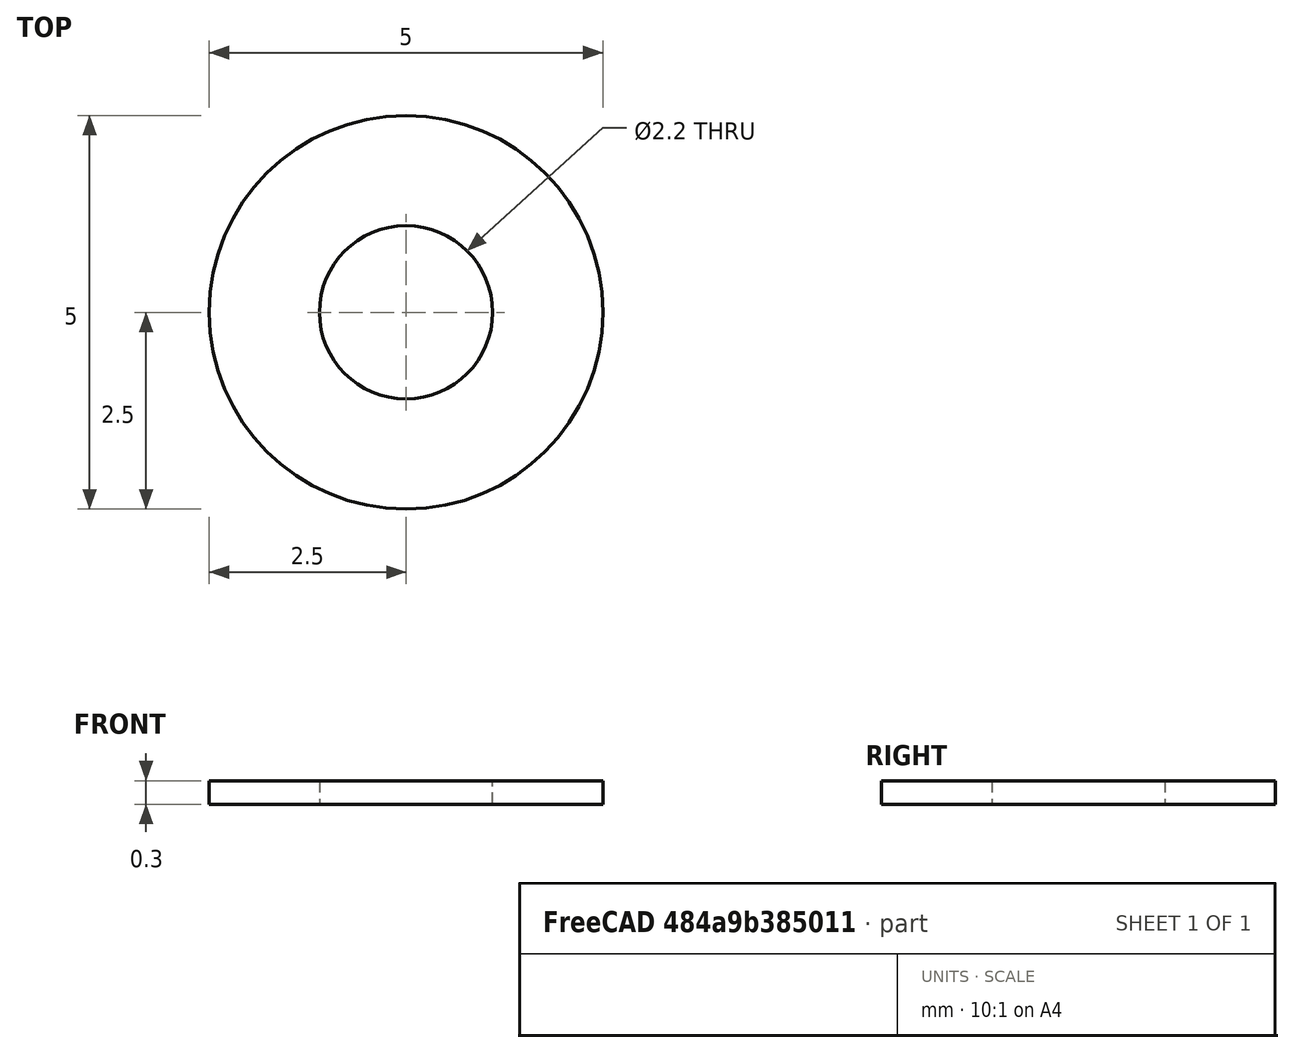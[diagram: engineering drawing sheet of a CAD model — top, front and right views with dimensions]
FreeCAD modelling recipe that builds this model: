
FCSTD DOCUMENT  (FreeCAD 1.0R39319 (Git))
Label: rondelleM2
License: All rights reserved
LicenseURL: https://en.wikipedia.org/wiki/All_rights_reserved
objects: Sketcher::SketchObject×1, PartDesign::Pad×1, PartDesign::Body×1
note: 6 computed .brp shape members not serialized (recipe doc carries the construction recipe); baked Part::Feature solids carry a one-line shape summary decoded from their .brp

FEATURE [Sketcher::SketchObject] Sketch
  ArcFitTolerance = 1e-06
  AttachmentSupport = -> [XY_Plane]
  FullyConstrained = true
  MakeInternals = false
  MapMode = 5
  sketch-geometry (2):
    g0: Circle CenterX=0 CenterY=0 CenterZ=0 NormalX=0 NormalY=0 NormalZ=1 AngleXU=0 Radius=1.1
    g1: Circle CenterX=0 CenterY=0 CenterZ=0 NormalX=0 NormalY=0 NormalZ=1 AngleXU=0 Radius=2.5
  constraints (4):
    c: Coincident(g0,g-1)
    c: Coincident(g1,g0)
    c: Diameter(g0) = 2.2
    c: Diameter(g1) = 5
FEATURE [PartDesign::Pad] Pad
  Direction = (0,0,1)
  Length = 0.3
  Length2 = 10
  Profile = -> Sketch
  ReferenceAxis = -> Sketch [N_Axis]
  Refine = true
  Suppressed = false
  Type = 0
FEATURE [PartDesign::Body] Body  label="Corps"
  AllowCompound = false
  Group = -> [Sketch,Pad]
  Origin = -> Origin
  Tip = -> Pad
